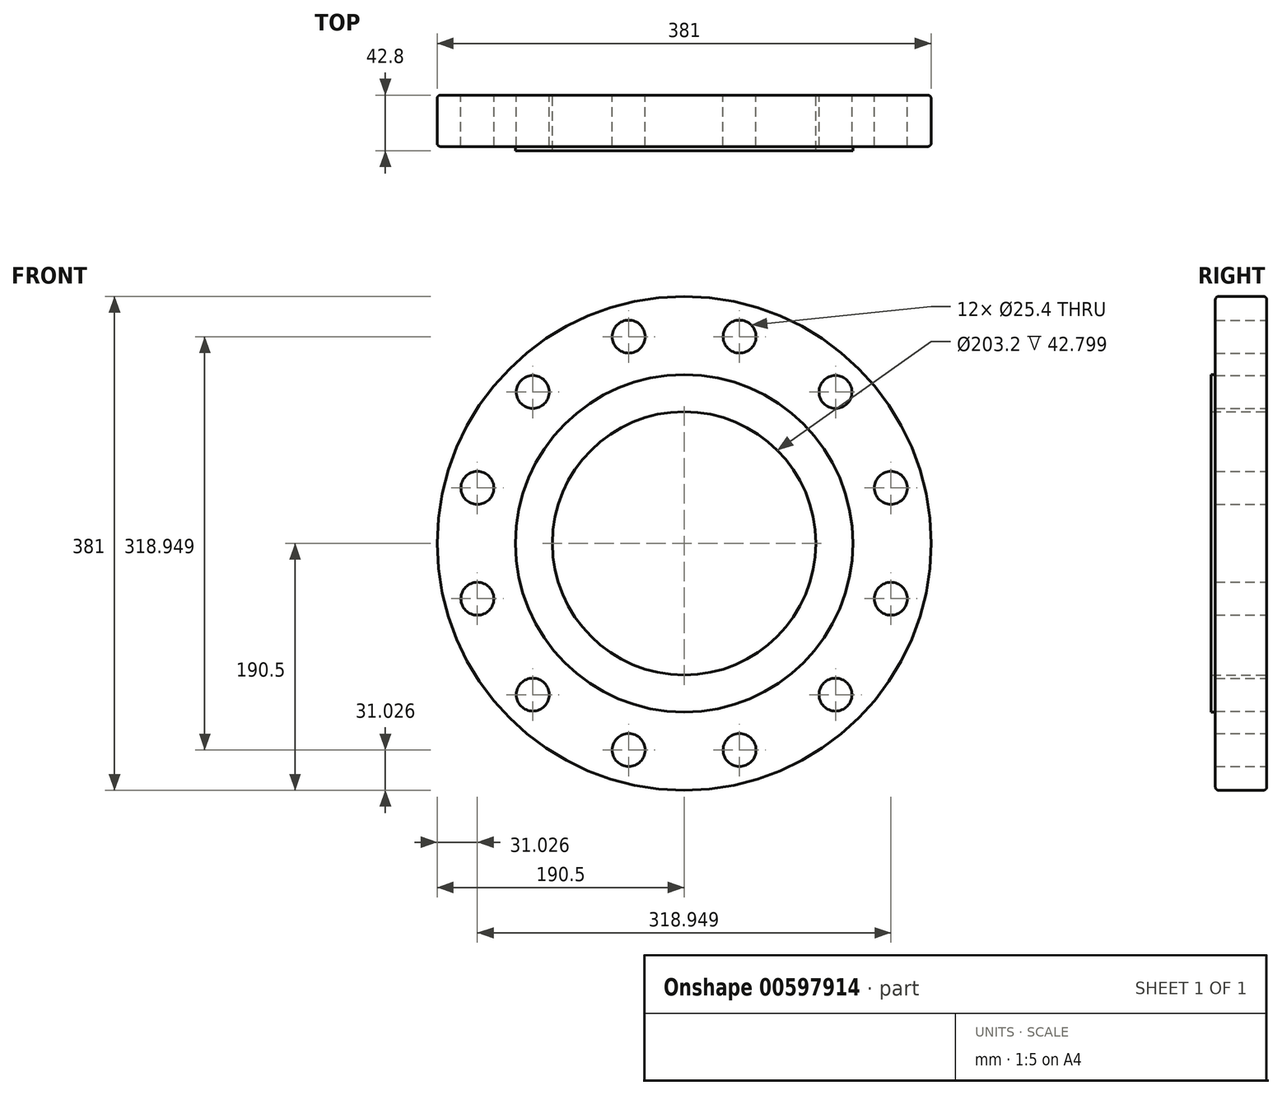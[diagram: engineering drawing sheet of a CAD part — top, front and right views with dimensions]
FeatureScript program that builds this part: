
annotation { "Feature Type Name" : "Feature", "Feature Type Description" : "" }
export const myFeature = defineFeature(function(context is Context, id is Id, definition is map)
    precondition{}
    {
        {
            var Q0;
            Q0=qCreatedBy(makeId("Front.planeOp"),FACE);
            var sketch = newSketch(context, id + "F0", { "sketchPlane" : qUnion([Q0])});
            skCircle(sketch, "E0", {"center": v(0, 0) * mm, "radius": 101.6 * mm});
            skCircle(sketch, "E1", {"center": v(0, 0) * mm, "radius": 190.5 * mm});
            skCircle(sketch, "E2", {"center": v(0, 0) * mm, "radius": 165.1 * mm, "construction": true});
            skCircle(sketch, "E3", {"center": v(42.73, 159.47) * mm, "radius": 12.7 * mm});
            skLineSegment(sketch, "E4", {"start": v(0, 0) * mm, "end": v(0, 261.76) * mm, "construction": true});
            skLineSegment(sketch, "E5", {"start": v(0, 0) * mm, "end": v(67.8, 253) * mm, "construction": true});
            skCircle(sketch, "E6.1.0", {"center": v(-42.73, 159.47) * mm, "radius": 12.7 * mm});
            skCircle(sketch, "E6.2.0", {"center": v(-116.74, 116.74) * mm, "radius": 12.7 * mm});
            skCircle(sketch, "E6.3.0", {"center": v(-159.47, 42.73) * mm, "radius": 12.7 * mm});
            skCircle(sketch, "E6.4.0", {"center": v(-159.47, -42.73) * mm, "radius": 12.7 * mm});
            skCircle(sketch, "E6.5.0", {"center": v(-116.74, -116.74) * mm, "radius": 12.7 * mm});
            skCircle(sketch, "E6.6.0", {"center": v(-42.73, -159.47) * mm, "radius": 12.7 * mm});
            skCircle(sketch, "E6.7.0", {"center": v(42.73, -159.47) * mm, "radius": 12.7 * mm});
            skCircle(sketch, "E6.8.0", {"center": v(116.74, -116.74) * mm, "radius": 12.7 * mm});
            skCircle(sketch, "E6.9.0", {"center": v(159.47, -42.73) * mm, "radius": 12.7 * mm});
            skCircle(sketch, "E6.10.0", {"center": v(159.47, 42.73) * mm, "radius": 12.7 * mm});
            skCircle(sketch, "E6.11.0", {"center": v(116.74, 116.74) * mm, "radius": 12.7 * mm});
            skSolve(sketch);
        }
        {
            var Q0;
            Q0 = qSketchRegion(id + "F0", true);
            extrude(context, id + "F1", {"entities" : qUnion([Q0]), "depth" : 39.62 * mm, "offsetDistance" : 25.4 * mm});
        }
        {
            var Q0;
            Q0=makeQuery(id+"F1.opExtrude","CAP_FACE",FACE,{"disambiguationData":[OSD([sQuery(id+"F0.wireOp",EDGE,"E0"),sQuery(id+"F0.wireOp",EDGE,"E1"),sQuery(id+"F0.wireOp",EDGE,"E3"),sQuery(id+"F0.wireOp",EDGE,"E6.1.0"),sQuery(id+"F0.wireOp",EDGE,"E6.2.0"),sQuery(id+"F0.wireOp",EDGE,"E6.3.0"),sQuery(id+"F0.wireOp",EDGE,"E6.4.0"),sQuery(id+"F0.wireOp",EDGE,"E6.5.0"),sQuery(id+"F0.wireOp",EDGE,"E6.6.0"),sQuery(id+"F0.wireOp",EDGE,"E6.7.0"),sQuery(id+"F0.wireOp",EDGE,"E6.8.0"),sQuery(id+"F0.wireOp",EDGE,"E6.9.0"),sQuery(id+"F0.wireOp",EDGE,"E6.10.0"),sQuery(id+"F0.wireOp",EDGE,"E6.11.0")])],"isStart":false});
            var sketch = newSketch(context, id + "F2", { "sketchPlane" : qUnion([Q0])});
            skCircle(sketch, "E7", {"center": v(0, 0) * mm, "radius": 101.6 * mm});
            skCircle(sketch, "E8", {"center": v(0, 0) * mm, "radius": 130.18 * mm});
            skSolve(sketch);
        }
        {
            var Q0;
            Q0 = qSketchRegion(id + "F2", true);
            extrude(context, id + "F3", {"entities" : qUnion([Q0]), "operationType" : NewBodyOperationType.ADD, "depth" : 3.17 * mm, "offsetDistance" : 25.4 * mm});
        }
        {
            var Q0;
            Q0=makeQuery(id+"F1.opExtrude","CAP_EDGE",EDGE,{"disambiguationData":[OSD([sQuery(id+"F0.wireOp",EDGE,"E1")])],"isStart":false});
            var Q1;
            Q1=makeQuery(id+"F1.opExtrude","CAP_EDGE",EDGE,{"disambiguationData":[OSD([sQuery(id+"F0.wireOp",EDGE,"E1")])],"isStart":true});
            var Q2;
            Q2=makeQuery(id+"F3.opExtrude","CAP_EDGE",EDGE,{"disambiguationData":[OSD([sQuery(id+"F2.wireOp",EDGE,"E8")])],"isStart":true});
            fillet(context, id + "F4", {"entities" : qUnion([Q0, Q1, Q2]), "radius" : 2.54 * mm, "tangentPropagation" : true, "allowEdgeOverflow" : false});
        }
    });
